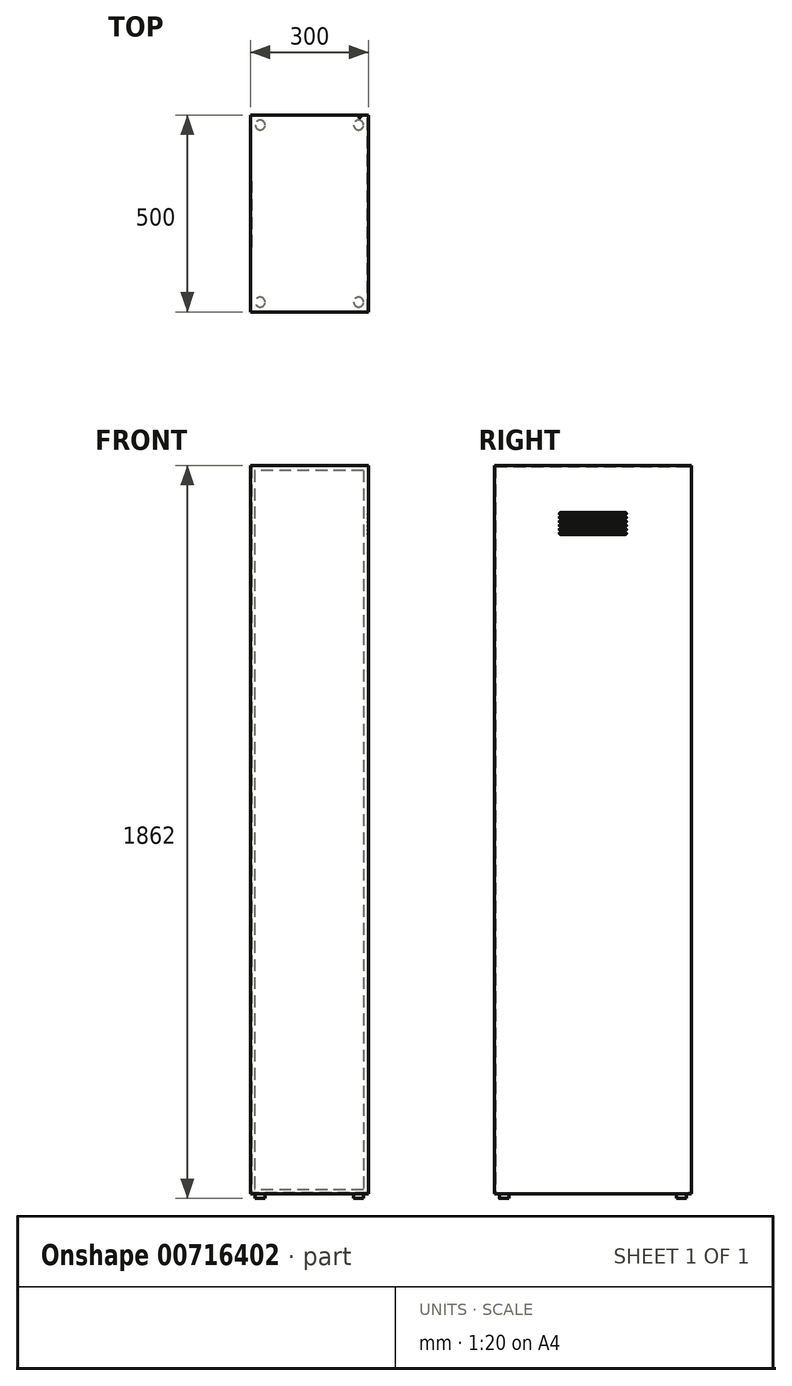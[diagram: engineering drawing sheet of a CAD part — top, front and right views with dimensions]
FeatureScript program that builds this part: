
annotation { "Feature Type Name" : "Feature", "Feature Type Description" : "" }
export const myFeature = defineFeature(function(context is Context, id is Id, definition is map)
    precondition{}
    {
        {
            var Q0;
            Q0=qCreatedBy(makeId("Top.planeOp"),FACE);
            var sketch = newSketch(context, id + "F0", { "sketchPlane" : qUnion([Q0])});
            skLineSegment(sketch, "E0.bottom", {"start": v(0, 0) * mm, "end": v(300, 0) * mm});
            skLineSegment(sketch, "E0.top", {"start": v(0, 500) * mm, "end": v(300, 500) * mm});
            skLineSegment(sketch, "E0.left", {"start": v(0, 0) * mm, "end": v(0, 500) * mm});
            skLineSegment(sketch, "E0.right", {"start": v(300, 0) * mm, "end": v(300, 500) * mm});
            skSolve(sketch);
        }
        {
            var Q0;
            Q0 = qSketchRegion(id + "F0", true);
            extrude(context, id + "F1", {"entities" : qUnion([Q0]), "depth" : 1850 * mm, "offsetDistance" : 25 * mm});
        }
        {
            var Q0;
            Q0=makeQuery(id+"F1.opExtrude","SWEPT_FACE",FACE,{"disambiguationData":[OSD([sQuery(id+"F0.wireOp",EDGE,"E0.top")])]});
            shell(context, id + "F2", {"entities" : qUnion([Q0]), "thickness" : 2.5 * mm});
        }
        {
            var Q0;
            Q0=makeQuery(id+"F1.opExtrude","SWEPT_FACE",FACE,{"disambiguationData":[OSD([sQuery(id+"F0.wireOp",EDGE,"E0.top")])]});
            var sketch = newSketch(context, id + "F3", { "sketchPlane" : qUnion([Q0])});
            skLineSegment(sketch, "E1.bottom", {"start": v(-297.5, 1847.5) * mm, "end": v(0, 1847.5) * mm});
            skLineSegment(sketch, "E1.top", {"start": v(-297.5, 0) * mm, "end": v(0, 0) * mm});
            skLineSegment(sketch, "E1.left", {"start": v(-297.5, 1847.5) * mm, "end": v(-297.5, 0) * mm});
            skLineSegment(sketch, "E1.right", {"start": v(0, 1847.5) * mm, "end": v(0, 0) * mm});
            skLineSegment(sketch, "E2.0", {"start": v(-10, 1837.5) * mm, "end": v(-10, 10) * mm});
            skLineSegment(sketch, "E2.1", {"start": v(-287.5, 1837.5) * mm, "end": v(-10, 1837.5) * mm});
            skLineSegment(sketch, "E2.2", {"start": v(-287.5, 1837.5) * mm, "end": v(-287.5, 10) * mm});
            skLineSegment(sketch, "E2.3", {"start": v(-287.5, 10) * mm, "end": v(-10, 10) * mm});
            skSolve(sketch);
        }
        {
            var Q0;
            Q0 = qSketchRegion(id + "F3", true);
            extrude(context, id + "F4", {"entities" : qUnion([Q0]), "operationType" : NewBodyOperationType.ADD, "oppositeDirection" : true, "depth" : 2.5 * mm, "offsetDistance" : 25 * mm});
        }
        {
            var Q0;
            Q0=makeQuery(id+"F1.opExtrude","CAP_FACE",FACE,{"disambiguationData":[OSD([sQuery(id+"F0.wireOp",EDGE,"E0.bottom"),sQuery(id+"F0.wireOp",EDGE,"E0.top"),sQuery(id+"F0.wireOp",EDGE,"E0.left"),sQuery(id+"F0.wireOp",EDGE,"E0.right")])],"isStart":true});
            var sketch = newSketch(context, id + "F5", { "sketchPlane" : qUnion([Q0])});
            skCircle(sketch, "E3", {"center": v(25, -25) * mm, "radius": 12.5 * mm});
            skCircle(sketch, "E4", {"center": v(25, -475) * mm, "radius": 12.5 * mm});
            skCircle(sketch, "E5", {"center": v(275, -25) * mm, "radius": 12.5 * mm});
            skCircle(sketch, "E6", {"center": v(275, -475) * mm, "radius": 12.5 * mm});
            skSolve(sketch);
        }
        {
            var Q0;
            Q0 = qSketchRegion(id + "F5", true);
            extrude(context, id + "F6", {"entities" : qUnion([Q0]), "operationType" : NewBodyOperationType.ADD, "depth" : 12 * mm, "offsetDistance" : 25 * mm});
        }
        {
            var Q0;
            Q0=makeQuery(id+"F1.opExtrude","CAP_FACE",FACE,{"disambiguationData":[OSD([sQuery(id+"F0.wireOp",EDGE,"E0.bottom"),sQuery(id+"F0.wireOp",EDGE,"E0.top"),sQuery(id+"F0.wireOp",EDGE,"E0.left"),sQuery(id+"F0.wireOp",EDGE,"E0.right")])],"isStart":false});
            var sketch = newSketch(context, id + "F7", { "sketchPlane" : qUnion([Q0])});
            skCircle(sketch, "E7", {"center": v(277.5, 495) * mm, "radius": 2 * mm});
            skSolve(sketch);
        }
        {
            var Q0;
            Q0=makeQuery(id+"F1.opExtrude","SWEPT_FACE",FACE,{"disambiguationData":[OSD([sQuery(id+"F0.wireOp",EDGE,"E0.left")])]});
            var sketch = newSketch(context, id + "F8", { "sketchPlane" : qUnion([Q0])});
            skLineSegment(sketch, "E8", {"start": v(-250, 1850) * mm, "end": v(-250, 0) * mm, "construction": true});
            skLineSegment(sketch, "E9.bottom", {"start": v(-333, 1730) * mm, "end": v(-167, 1730) * mm});
            skLineSegment(sketch, "E9.top", {"start": v(-333, 1725) * mm, "end": v(-167, 1725) * mm});
            skLineSegment(sketch, "E9.left", {"start": v(-335, 1728) * mm, "end": v(-335, 1727) * mm});
            skLineSegment(sketch, "E9.right", {"start": v(-165, 1728) * mm, "end": v(-165, 1727) * mm});
            skPoint(sketch, "E10.visualSharp", {"position": v(-335, 1730) * mm});
            skArc(sketch, "E10.filletArc", {"start": v(-333, 1730) * mm, "mid": v(-334.41, 1729.41) * mm, "end": v(-335, 1728) * mm});
            skPoint(sketch, "E11.visualSharp", {"position": v(-335, 1725) * mm});
            skArc(sketch, "E11.filletArc", {"start": v(-335, 1727) * mm, "mid": v(-334.41, 1725.59) * mm, "end": v(-333, 1725) * mm});
            skPoint(sketch, "E12.visualSharp", {"position": v(-165, 1730) * mm});
            skArc(sketch, "E12.filletArc", {"start": v(-165, 1728) * mm, "mid": v(-165.59, 1729.41) * mm, "end": v(-167, 1730) * mm});
            skPoint(sketch, "E13.visualSharp", {"position": v(-165, 1725) * mm});
            skArc(sketch, "E13.filletArc", {"start": v(-167, 1725) * mm, "mid": v(-165.59, 1725.59) * mm, "end": v(-165, 1727) * mm});
            skPoint(sketch, "E14.1.0.0", {"position": v(-165, 1715) * mm});
            skLineSegment(sketch, "E14.1.0.1", {"start": v(-333, 1715) * mm, "end": v(-167, 1715) * mm});
            skLineSegment(sketch, "E14.1.0.2", {"start": v(-333, 1720) * mm, "end": v(-167, 1720) * mm});
            skPoint(sketch, "E14.1.0.3", {"position": v(-335, 1720) * mm});
            skPoint(sketch, "E14.1.0.4", {"position": v(-335, 1715) * mm});
            skPoint(sketch, "E14.1.0.5", {"position": v(-165, 1720) * mm});
            skArc(sketch, "E14.1.0.6", {"start": v(-165, 1718) * mm, "mid": v(-165.59, 1719.41) * mm, "end": v(-167, 1720) * mm});
            skArc(sketch, "E14.1.0.7", {"start": v(-333, 1720) * mm, "mid": v(-334.41, 1719.41) * mm, "end": v(-335, 1718) * mm});
            skArc(sketch, "E14.1.0.8", {"start": v(-335, 1717) * mm, "mid": v(-334.41, 1715.59) * mm, "end": v(-333, 1715) * mm});
            skArc(sketch, "E14.1.0.9", {"start": v(-167, 1715) * mm, "mid": v(-165.59, 1715.59) * mm, "end": v(-165, 1717) * mm});
            skLineSegment(sketch, "E14.1.0.10", {"start": v(-335, 1718) * mm, "end": v(-335, 1717) * mm});
            skLineSegment(sketch, "E14.1.0.11", {"start": v(-165, 1718) * mm, "end": v(-165, 1717) * mm});
            skPoint(sketch, "E14.2.0.0", {"position": v(-165, 1705) * mm});
            skLineSegment(sketch, "E14.2.0.1", {"start": v(-333, 1705) * mm, "end": v(-167, 1705) * mm});
            skLineSegment(sketch, "E14.2.0.2", {"start": v(-333, 1710) * mm, "end": v(-167, 1710) * mm});
            skPoint(sketch, "E14.2.0.3", {"position": v(-335, 1710) * mm});
            skPoint(sketch, "E14.2.0.4", {"position": v(-335, 1705) * mm});
            skPoint(sketch, "E14.2.0.5", {"position": v(-165, 1710) * mm});
            skArc(sketch, "E14.2.0.6", {"start": v(-165, 1708) * mm, "mid": v(-165.59, 1709.41) * mm, "end": v(-167, 1710) * mm});
            skArc(sketch, "E14.2.0.7", {"start": v(-333, 1710) * mm, "mid": v(-334.41, 1709.41) * mm, "end": v(-335, 1708) * mm});
            skArc(sketch, "E14.2.0.8", {"start": v(-335, 1707) * mm, "mid": v(-334.41, 1705.59) * mm, "end": v(-333, 1705) * mm});
            skArc(sketch, "E14.2.0.9", {"start": v(-167, 1705) * mm, "mid": v(-165.59, 1705.59) * mm, "end": v(-165, 1707) * mm});
            skLineSegment(sketch, "E14.2.0.10", {"start": v(-335, 1708) * mm, "end": v(-335, 1707) * mm});
            skLineSegment(sketch, "E14.2.0.11", {"start": v(-165, 1708) * mm, "end": v(-165, 1707) * mm});
            skPoint(sketch, "E14.3.0.0", {"position": v(-165, 1695) * mm});
            skLineSegment(sketch, "E14.3.0.1", {"start": v(-333, 1695) * mm, "end": v(-167, 1695) * mm});
            skLineSegment(sketch, "E14.3.0.2", {"start": v(-333, 1700) * mm, "end": v(-167, 1700) * mm});
            skPoint(sketch, "E14.3.0.3", {"position": v(-335, 1700) * mm});
            skPoint(sketch, "E14.3.0.4", {"position": v(-335, 1695) * mm});
            skPoint(sketch, "E14.3.0.5", {"position": v(-165, 1700) * mm});
            skArc(sketch, "E14.3.0.6", {"start": v(-165, 1698) * mm, "mid": v(-165.59, 1699.41) * mm, "end": v(-167, 1700) * mm});
            skArc(sketch, "E14.3.0.7", {"start": v(-333, 1700) * mm, "mid": v(-334.41, 1699.41) * mm, "end": v(-335, 1698) * mm});
            skArc(sketch, "E14.3.0.8", {"start": v(-335, 1697) * mm, "mid": v(-334.41, 1695.59) * mm, "end": v(-333, 1695) * mm});
            skArc(sketch, "E14.3.0.9", {"start": v(-167, 1695) * mm, "mid": v(-165.59, 1695.59) * mm, "end": v(-165, 1697) * mm});
            skLineSegment(sketch, "E14.3.0.10", {"start": v(-335, 1698) * mm, "end": v(-335, 1697) * mm});
            skLineSegment(sketch, "E14.3.0.11", {"start": v(-165, 1698) * mm, "end": v(-165, 1697) * mm});
            skPoint(sketch, "E14.4.0.0", {"position": v(-165, 1685) * mm});
            skLineSegment(sketch, "E14.4.0.1", {"start": v(-333, 1685) * mm, "end": v(-167, 1685) * mm});
            skLineSegment(sketch, "E14.4.0.2", {"start": v(-333, 1690) * mm, "end": v(-167, 1690) * mm});
            skPoint(sketch, "E14.4.0.3", {"position": v(-335, 1690) * mm});
            skPoint(sketch, "E14.4.0.4", {"position": v(-335, 1685) * mm});
            skPoint(sketch, "E14.4.0.5", {"position": v(-165, 1690) * mm});
            skArc(sketch, "E14.4.0.6", {"start": v(-165, 1688) * mm, "mid": v(-165.59, 1689.41) * mm, "end": v(-167, 1690) * mm});
            skArc(sketch, "E14.4.0.7", {"start": v(-333, 1690) * mm, "mid": v(-334.41, 1689.41) * mm, "end": v(-335, 1688) * mm});
            skArc(sketch, "E14.4.0.8", {"start": v(-335, 1687) * mm, "mid": v(-334.41, 1685.59) * mm, "end": v(-333, 1685) * mm});
            skArc(sketch, "E14.4.0.9", {"start": v(-167, 1685) * mm, "mid": v(-165.59, 1685.59) * mm, "end": v(-165, 1687) * mm});
            skLineSegment(sketch, "E14.4.0.10", {"start": v(-335, 1688) * mm, "end": v(-335, 1687) * mm});
            skLineSegment(sketch, "E14.4.0.11", {"start": v(-165, 1688) * mm, "end": v(-165, 1687) * mm});
            skPoint(sketch, "E14.5.0.0", {"position": v(-165, 1675) * mm});
            skLineSegment(sketch, "E14.5.0.1", {"start": v(-333, 1675) * mm, "end": v(-167, 1675) * mm});
            skLineSegment(sketch, "E14.5.0.2", {"start": v(-333, 1680) * mm, "end": v(-167, 1680) * mm});
            skPoint(sketch, "E14.5.0.3", {"position": v(-335, 1680) * mm});
            skPoint(sketch, "E14.5.0.4", {"position": v(-335, 1675) * mm});
            skPoint(sketch, "E14.5.0.5", {"position": v(-165, 1680) * mm});
            skArc(sketch, "E14.5.0.6", {"start": v(-165, 1678) * mm, "mid": v(-165.59, 1679.41) * mm, "end": v(-167, 1680) * mm});
            skArc(sketch, "E14.5.0.7", {"start": v(-333, 1680) * mm, "mid": v(-334.41, 1679.41) * mm, "end": v(-335, 1678) * mm});
            skArc(sketch, "E14.5.0.8", {"start": v(-335, 1677) * mm, "mid": v(-334.41, 1675.59) * mm, "end": v(-333, 1675) * mm});
            skArc(sketch, "E14.5.0.9", {"start": v(-167, 1675) * mm, "mid": v(-165.59, 1675.59) * mm, "end": v(-165, 1677) * mm});
            skLineSegment(sketch, "E14.5.0.10", {"start": v(-335, 1678) * mm, "end": v(-335, 1677) * mm});
            skLineSegment(sketch, "E14.5.0.11", {"start": v(-165, 1678) * mm, "end": v(-165, 1677) * mm});
            skLineSegment(sketch, "E14.direction1", {"start": v(-335, 1725) * mm, "end": v(-335, 1715) * mm, "construction": true});
            skSolve(sketch);
        }
        {
            var Q0;
            Q0 = qSketchRegion(id + "F8", true);
            extrude(context, id + "F9", {"entities" : qUnion([Q0]), "operationType" : NewBodyOperationType.REMOVE, "endBound" : BoundingType.THROUGH_ALL, "oppositeDirection" : true, "depth" : 25 * mm, "offsetDistance" : 25 * mm});
        }
        {
            var Q0;
            Q0 = qSketchRegion(id + "F7", true);
            extrude(context, id + "F10", {"entities" : qUnion([Q0]), "operationType" : NewBodyOperationType.REMOVE, "endBound" : BoundingType.THROUGH_ALL, "oppositeDirection" : true, "depth" : 25 * mm, "offsetDistance" : 25 * mm});
        }
    });
